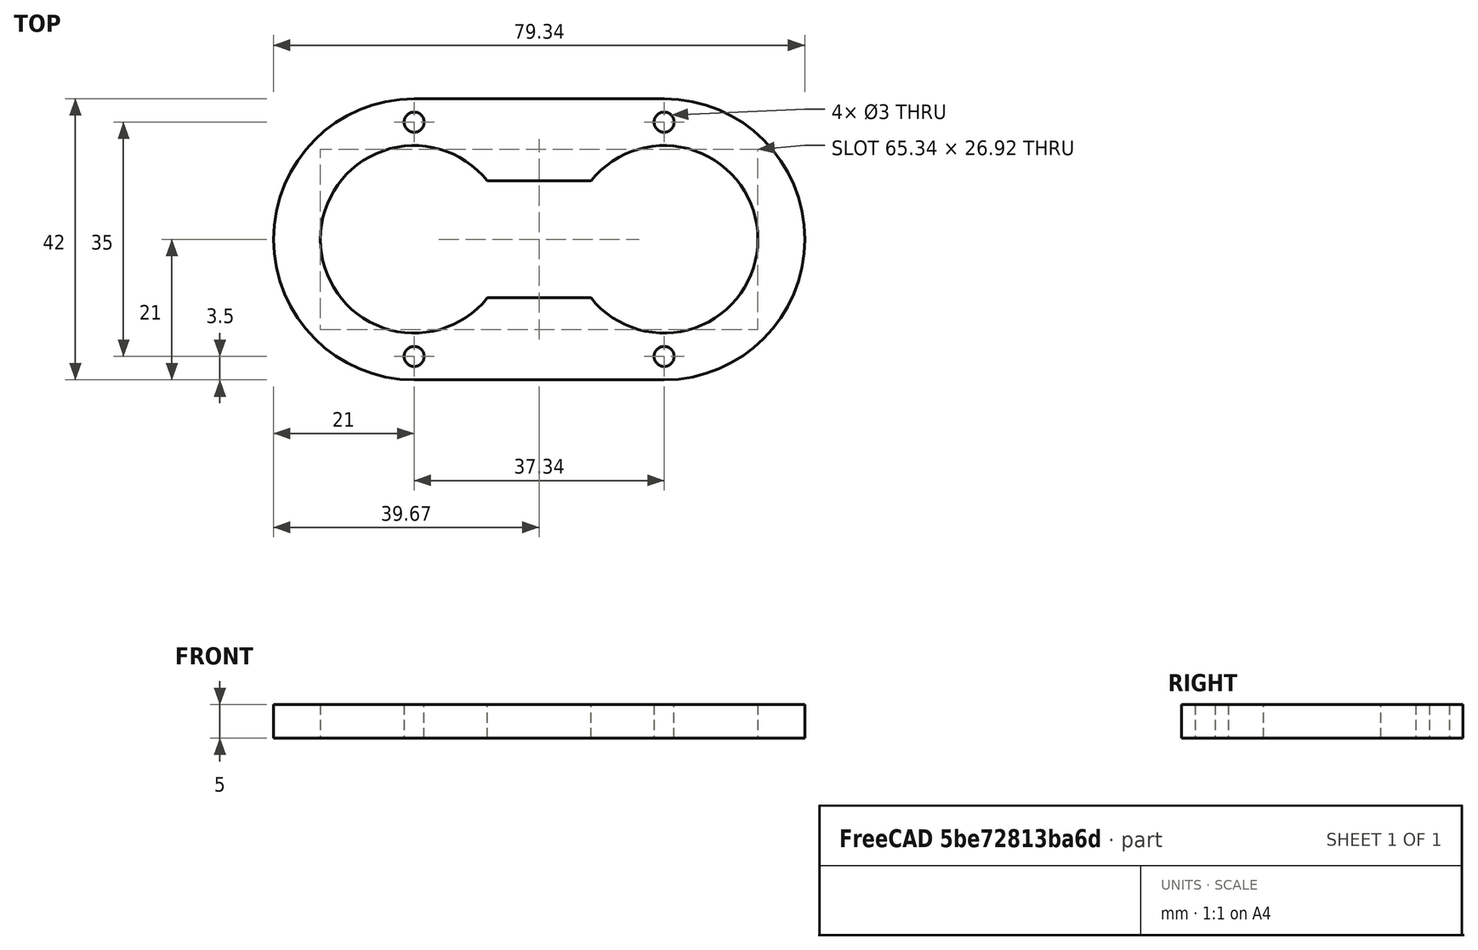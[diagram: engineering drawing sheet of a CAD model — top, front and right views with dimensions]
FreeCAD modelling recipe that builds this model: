
FCSTD DOCUMENT  (FreeCAD 0.16R6706 (Git))
Label: parametric_plaque
License: All rights reserved
LicenseURL: http://en.wikipedia.org/wiki/All_rights_reserved
objects: Spreadsheet::Sheet×1, Sketcher::SketchObject×1, PartDesign::Pad×1
note: 3 computed .brp shape members not serialized (recipe doc carries the construction recipe); baked Part::Feature solids carry a one-line shape summary decoded from their .brp

FEATURE [Spreadsheet::Sheet] Spreadsheet  label="Parameters"
  cells = A1=Parametric Plate Parameters; B2=Model; C2=3D printed; D2=Radiant Dyes; E2=Thorlabs KM100; F2=Liop-Tec; A3=Plaque axis distance; B3(L)=53.3; C3=54; D3=43.8; E3=53.3; F3=49; A10=
FEATURE [Sketcher::SketchObject] Sketch
  expr: Constraints[3] = Parameters.L - 16
  sketch-geometry (16):
    g0: LineSegment [constr] StartX=-18.65 StartY=70.9443 StartZ=0 EndX=-18.65 EndY=-70.9443 EndZ=0
    g1: LineSegment [constr] StartX=18.65 StartY=70.9443 StartZ=0 EndX=18.65 EndY=-70.9443 EndZ=0
    g2: LineSegment StartX=-18.65 StartY=21 StartZ=0 EndX=18.65 EndY=21 EndZ=0
    g3: LineSegment StartX=18.65 StartY=-21 StartZ=0 EndX=-18.65 EndY=-21 EndZ=0
    g4: ArcOfCircle CenterX=-18.65 CenterY=0 CenterZ=0 NormalX=0 NormalY=0 NormalZ=1 Radius=21 StartAngle=1.5708 EndAngle=4.71239
    g5: ArcOfCircle CenterX=18.65 CenterY=0 CenterZ=0 NormalX=0 NormalY=0 NormalZ=1 Radius=21 StartAngle=4.71239 EndAngle=7.85398
    g6: ArcOfCircle CenterX=-18.65 CenterY=0 CenterZ=0 NormalX=0 NormalY=0 NormalZ=1 Radius=14 StartAngle=0.675132 EndAngle=5.60805
    g7: ArcOfCircle CenterX=18.65 CenterY=0 CenterZ=0 NormalX=0 NormalY=0 NormalZ=1 Radius=14 StartAngle=3.81672 EndAngle=8.74965
    g8: LineSegment StartX=-7.72125 StartY=8.75 StartZ=0 EndX=7.72125 EndY=8.75 EndZ=0
    g9: LineSegment StartX=7.72125 StartY=-8.75 StartZ=0 EndX=-7.72125 EndY=-8.75 EndZ=0
    g10: LineSegment [constr] StartX=-18.65 StartY=-17.5 StartZ=0 EndX=18.65 EndY=-17.5 EndZ=0
    g11: LineSegment [constr] StartX=18.65 StartY=17.5 StartZ=0 EndX=-18.65 EndY=17.5 EndZ=0
    g12: Circle CenterX=-18.65 CenterY=17.5 CenterZ=0 NormalX=0 NormalY=0 NormalZ=1 Radius=1.5
    g13: Circle CenterX=18.65 CenterY=17.5 CenterZ=0 NormalX=0 NormalY=0 NormalZ=1 Radius=1.5
    g14: Circle CenterX=-18.65 CenterY=-17.5 CenterZ=0 NormalX=0 NormalY=0 NormalZ=1 Radius=1.5
    g15: Circle CenterX=18.65 CenterY=-17.5 CenterZ=0 NormalX=0 NormalY=0 NormalZ=1 Radius=1.5
  constraints (48):
    c: Symmetric(g0,g0,g-1)
    c: Symmetric(g1,g1,g-1)
    c: Symmetric(g1,g0,g-2)
    c: DistanceX(g0,g1) = 37.3
    c: PointOnObject(g2,g0)
    c: PointOnObject(g2,g1)
    c: Horizontal(g2)
    c: PointOnObject(g3,g1)
    c: PointOnObject(g3,g0)
    c: Horizontal(g3)
    c: Symmetric(g2,g3,g-1)
    c: DistanceY(g3,g2) = 42
    c: Coincident(g4,g2)
    c: Coincident(g4,g3)
    c: Coincident(g5,g2)
    c: Coincident(g5,g3)
    c: PointOnObject(g4,g0)
    c: PointOnObject(g5,g1)
    c: PointOnObject(g6,g-1)
    c: PointOnObject(g6,g0)
    c: PointOnObject(g7,g1)
    c: Coincident(g8,g6)
    c: Coincident(g8,g7)
    c: Horizontal(g8)
    c: Coincident(g9,g7)
    c: Coincident(g9,g6)
    c: Horizontal(g9)
    c: Symmetric(g6,g6,g-1)
    c: DistanceY(g7,g7) = 17.5
    c: Radius(g6) = 14
    c: Equal(g6,g7)
    c: PointOnObject(g7,g-1)
    c: PointOnObject(g10,g0)
    c: PointOnObject(g10,g1)
    c: Horizontal(g10)
    c: PointOnObject(g11,g0)
    c: Horizontal(g11)
    c: Symmetric(g11,g10,g-1)
    c: DistanceY(g10,g11) = 35
    c: Coincident(g12,g11)
    c: Coincident(g13,g11)
    c: Coincident(g14,g10)
    c: Coincident(g15,g10)
    c: Radius(g14) = 1.5
    c: Equal(g14,g12)
    c: Equal(g14,g13)
    c: Equal(g14,g15)
    c: PointOnObject(g11,g1)
FEATURE [PartDesign::Pad] Pad  label="Plaque"
  Length = 5
  Length2 = 100
  Midplane = true
  Type = 0
